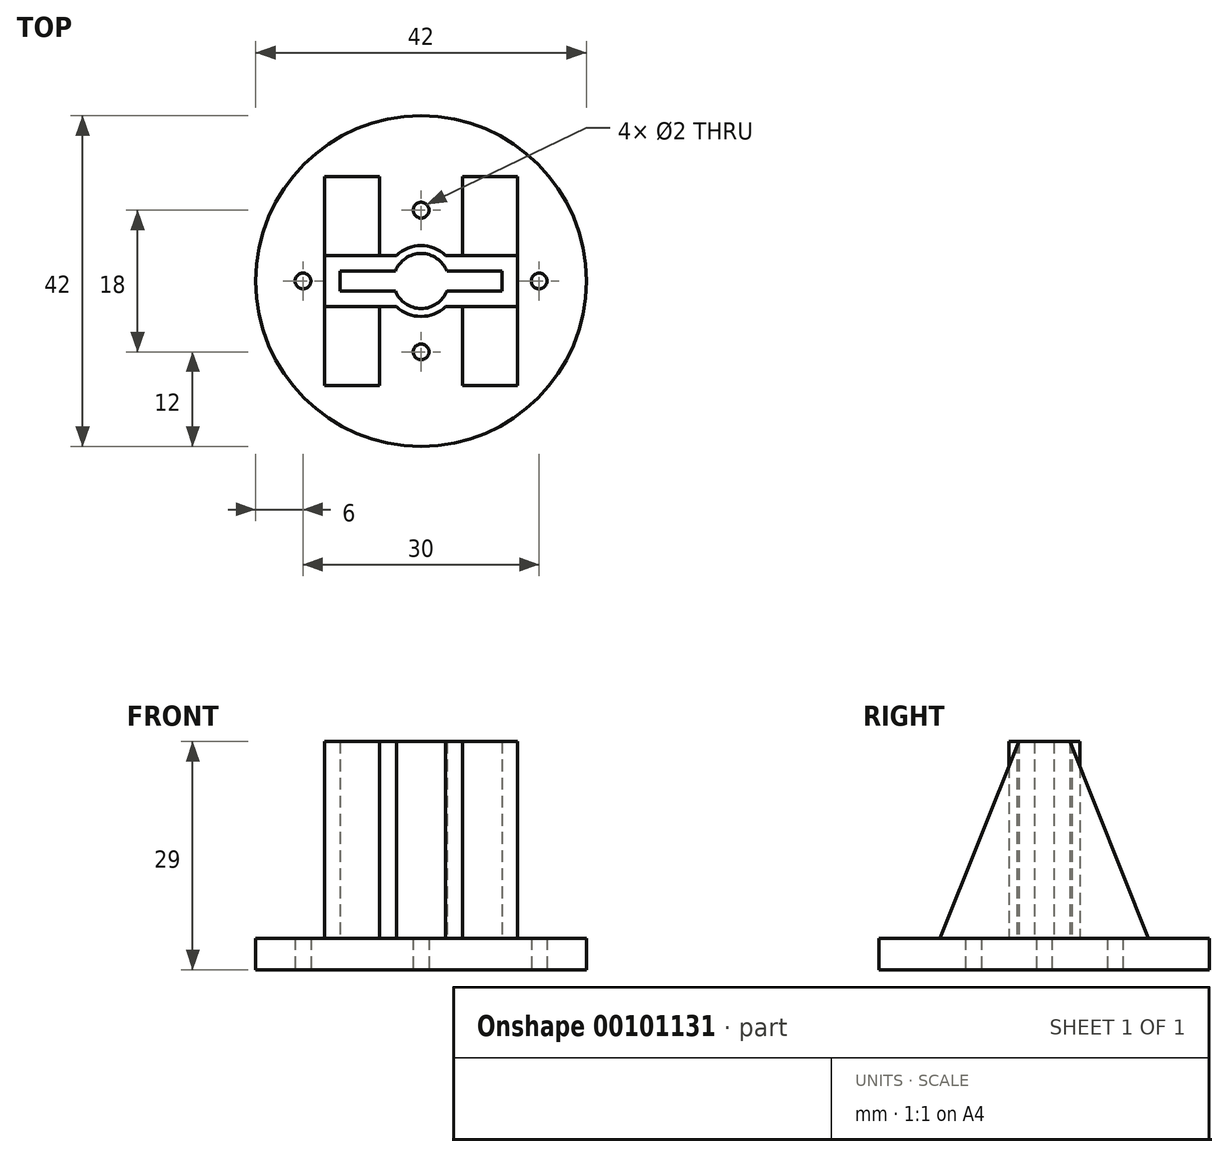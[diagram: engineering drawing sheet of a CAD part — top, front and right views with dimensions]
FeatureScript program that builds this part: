
annotation { "Feature Type Name" : "Feature", "Feature Type Description" : "" }
export const myFeature = defineFeature(function(context is Context, id is Id, definition is map)
    precondition{}
    {
        {
            var Q0;
            Q0=qCreatedBy(makeId("Top.planeOp"),FACE);
            var sketch = newSketch(context, id + "F0", { "sketchPlane" : qUnion([Q0])});
            skPoint(sketch, "E0", {"position": v(0, 9) * mm});
            skPoint(sketch, "E1", {"position": v(-15, 0) * mm});
            skPoint(sketch, "E2", {"position": v(15, 0) * mm});
            skPoint(sketch, "E3", {"position": v(0, -9) * mm});
            skCircle(sketch, "E4", {"center": v(0, 0) * mm, "radius": 21 * mm});
            skSolve(sketch);
        }
        {
            var Q0;
            Q0 = qSketchRegion(id + "F0", true);
            extrude(context, id + "F1", {"entities" : qUnion([Q0]), "depth" : 4 * mm});
        }
        {
            var Q0;
            Q0=sQuery(id+"F0.wireOp",VERTEX,"E1");
            var Q1;
            Q1=sQuery(id+"F0.wireOp",VERTEX,"E3");
            var Q2;
            Q2=sQuery(id+"F0.wireOp",VERTEX,"E0");
            var Q3;
            Q3=sQuery(id+"F0.wireOp",VERTEX,"E2");
            var Q4;
            Q4=makeQuery(id+"F1.opExtrude","SWEPT_BODY",BODY,{"disambiguationData":[OSD([sQuery(id+"F0.wireOp",EDGE,"E4")])]});
            hole(context, id + "F2", {"style" : HoleStyle.SIMPLE, "endStyle" : HoleEndStyle.THROUGH, "oppositeDirection" : true, "holeDiameter" : 2 * mm, "locations" : qUnion([Q0, Q1, Q2, Q3]), "scope" : qUnion([Q4]), "isTappedThrough" : true});
        }
        {
            var Q0;
            Q0=makeQuery(id+"F1.opExtrude","CAP_FACE",FACE,{"disambiguationData":[OSD([sQuery(id+"F0.wireOp",EDGE,"E4")])],"isStart":false});
            var sketch = newSketch(context, id + "F3", { "sketchPlane" : qUnion([Q0])});
            skCircle(sketch, "E5", {"center": v(0, 0) * mm, "radius": 3.5 * mm});
            skLineSegment(sketch, "E6", {"start": v(-3.27, 1.25) * mm, "end": v(-10.27, 1.25) * mm});
            skLineSegment(sketch, "E7", {"start": v(-10.27, 1.25) * mm, "end": v(-10.27, -1.25) * mm});
            skLineSegment(sketch, "E8", {"start": v(-10.27, -1.25) * mm, "end": v(-3.27, -1.25) * mm});
            skLineSegment(sketch, "E9.MirrorCS", {"start": v(3.27, 1.25) * mm, "end": v(10.27, 1.25) * mm});
            skLineSegment(sketch, "E10.MirrorCS", {"start": v(10.27, 1.25) * mm, "end": v(10.27, -1.25) * mm});
            skLineSegment(sketch, "E11.MirrorCS", {"start": v(10.27, -1.25) * mm, "end": v(3.27, -1.25) * mm});
            skCircle(sketch, "E12", {"center": v(0, 0) * mm, "radius": 4.5 * mm});
            skLineSegment(sketch, "E13", {"start": v(-1.3, -3.25) * mm, "end": v(-12.27, -3.25) * mm});
            skLineSegment(sketch, "E14", {"start": v(-12.27, -3.25) * mm, "end": v(-12.27, 3.25) * mm});
            skLineSegment(sketch, "E15", {"start": v(-12.27, 3.25) * mm, "end": v(-1.3, 3.25) * mm});
            skLineSegment(sketch, "E16.MirrorCS", {"start": v(12.27, 3.25) * mm, "end": v(1.3, 3.25) * mm});
            skLineSegment(sketch, "E17.MirrorCS", {"start": v(12.27, -3.25) * mm, "end": v(12.27, 3.25) * mm});
            skLineSegment(sketch, "E18.MirrorCS", {"start": v(1.3, -3.25) * mm, "end": v(12.27, -3.25) * mm});
            skSolve(sketch);
        }
        {
            var Q0;
            {var subQ6=sQuery(id+"F3.wireOp",EDGE,"E7");Q0=makeQuery(id+"F3.imprint","IMPRINT",FACE,{"disambiguationData":[TD([[makeQuery(id+"F3.imprint","IMPRINT",EDGE,{"derivedFrom":subQ6}),-1.0]])]});}
            var Q1;
            {var subQ0=sQuery(id+"F3.wireOp",EDGE,"E15");var subQ1=sQuery(id+"F3.wireOp",EDGE,"E5");var subQ2=makeQuery(id+"F3.imprint","INTERSECT",VERTEX,{"derivedFrom":[subQ1,subQ0]});Q1=makeQuery(id+"F3.imprint","IMPRINT",FACE,{"disambiguationData":[TD([[makeQuery(id+"F3.imprint","IMPRINT",EDGE,{"disambiguationData":[TD([[subQ2,1.0]])],"derivedFrom":subQ1}),-1.0]])]});}
            var Q2;
            {var subQ0=sQuery(id+"F3.wireOp",EDGE,"E6");var subQ1=sQuery(id+"F3.wireOp",EDGE,"E5");var subQ2=makeQuery(id+"F3.imprint","INTERSECT",VERTEX,{"derivedFrom":[subQ1,subQ0]});Q2=makeQuery(id+"F3.imprint","IMPRINT",FACE,{"disambiguationData":[TD([[makeQuery(id+"F3.imprint","IMPRINT",EDGE,{"disambiguationData":[TD([[subQ2,1.0]])],"derivedFrom":subQ1}),-1.0]])]});}
            var Q3;
            {var subQ0=sQuery(id+"F3.wireOp",EDGE,"E8");var subQ1=sQuery(id+"F3.wireOp",EDGE,"E5");var subQ2=makeQuery(id+"F3.imprint","INTERSECT",VERTEX,{"derivedFrom":[subQ1,subQ0]});Q3=makeQuery(id+"F3.imprint","IMPRINT",FACE,{"disambiguationData":[TD([[makeQuery(id+"F3.imprint","IMPRINT",EDGE,{"disambiguationData":[TD([[subQ2,-1.0]])],"derivedFrom":subQ1}),-1.0]])]});}
            var Q4;
            {var subQ0=sQuery(id+"F3.wireOp",EDGE,"E13");var subQ1=sQuery(id+"F3.wireOp",EDGE,"E5");var subQ2=makeQuery(id+"F3.imprint","INTERSECT",VERTEX,{"derivedFrom":[subQ1,subQ0]});Q4=makeQuery(id+"F3.imprint","IMPRINT",FACE,{"disambiguationData":[TD([[makeQuery(id+"F3.imprint","IMPRINT",EDGE,{"disambiguationData":[TD([[subQ2,-1.0]])],"derivedFrom":subQ1}),-1.0]])]});}
            var Q5;
            {var subQ0=sQuery(id+"F3.wireOp",EDGE,"E11.MirrorCS");var subQ1=sQuery(id+"F3.wireOp",EDGE,"E5");var subQ2=makeQuery(id+"F3.imprint","INTERSECT",VERTEX,{"derivedFrom":[subQ1,subQ0]});Q5=makeQuery(id+"F3.imprint","IMPRINT",FACE,{"disambiguationData":[TD([[makeQuery(id+"F3.imprint","IMPRINT",EDGE,{"disambiguationData":[TD([[subQ2,1.0]])],"derivedFrom":subQ1}),-1.0]])]});}
            var Q6;
            {var subQ0=sQuery(id+"F3.wireOp",EDGE,"E9.MirrorCS");var subQ1=sQuery(id+"F3.wireOp",EDGE,"E5");var subQ2=makeQuery(id+"F3.imprint","INTERSECT",VERTEX,{"derivedFrom":[subQ1,subQ0]});Q6=makeQuery(id+"F3.imprint","IMPRINT",FACE,{"disambiguationData":[TD([[makeQuery(id+"F3.imprint","IMPRINT",EDGE,{"disambiguationData":[TD([[subQ2,-1.0]])],"derivedFrom":subQ1}),-1.0]])]});}
            var Q7;
            {var subQ5=sQuery(id+"F3.wireOp",EDGE,"E10.MirrorCS");Q7=makeQuery(id+"F3.imprint","IMPRINT",FACE,{"disambiguationData":[TD([[makeQuery(id+"F3.imprint","IMPRINT",EDGE,{"derivedFrom":subQ5}),1.0]])]});}
            extrude(context, id + "F4", {"entities" : qUnion([Q0, Q1, Q2, Q3, Q4, Q5, Q6, Q7]), "operationType" : NewBodyOperationType.ADD, "depth" : 25 * mm});
        }
        {
            var Q0;
            Q0=makeQuery(id+"F4.opExtrude","SWEPT_FACE",FACE,{"disambiguationData":[OSD([sQuery(id+"F3.wireOp",EDGE,"E17.MirrorCS")])]});
            var sketch = newSketch(context, id + "F5", { "sketchPlane" : qUnion([Q0])});
            skLineSegment(sketch, "E19", {"start": v(-3.25, 29) * mm, "end": v(-13.25, 4) * mm});
            skLineSegment(sketch, "E20", {"start": v(-13.25, 4) * mm, "end": v(-3.25, 4) * mm});
            skLineSegment(sketch, "E21.MirrorCS", {"start": v(3.25, 29) * mm, "end": v(13.25, 4) * mm});
            skLineSegment(sketch, "E22.MirrorCS", {"start": v(13.25, 4) * mm, "end": v(3.25, 4) * mm});
            skSolve(sketch);
        }
        {
            var Q0;
            Q0=makeQuery(id+"F5.imprint","IMPRINT",FACE,{"disambiguationData":[TD([[makeQuery(id+"F5.imprint","IMPRINT",EDGE,{"derivedFrom":sQuery(id+"F5.wireOp",EDGE,"E19")}),1.0]])]});
            var Q1;
            Q1=makeQuery(id+"F5.imprint","IMPRINT",FACE,{"disambiguationData":[TD([[makeQuery(id+"F5.imprint","IMPRINT",EDGE,{"derivedFrom":sQuery(id+"F5.wireOp",EDGE,"E21.MirrorCS")}),-1.0]])]});
            extrude(context, id + "F6", {"entities" : qUnion([Q0, Q1]), "oppositeDirection" : true, "depth" : 7 * mm});
        }
        {
            var Q0;
            Q0=makeQuery(id+"F6.opExtrude","SWEPT_BODY",BODY,{"disambiguationData":[OSD([sQuery(id+"F3.wireOp",EDGE,"E17.MirrorCS"),sQuery(id+"F3.wireOp",EDGE,"E18.MirrorCS"),sQuery(id+"F5.wireOp",EDGE,"E19"),sQuery(id+"F5.wireOp",EDGE,"E20")])]});
            var Q1;
            Q1=makeQuery(id+"F6.opExtrude","SWEPT_BODY",BODY,{"disambiguationData":[OSD([sQuery(id+"F3.wireOp",EDGE,"E16.MirrorCS"),sQuery(id+"F3.wireOp",EDGE,"E17.MirrorCS"),sQuery(id+"F5.wireOp",EDGE,"E21.MirrorCS"),sQuery(id+"F5.wireOp",EDGE,"E22.MirrorCS")])]});
            var Q2;
            Q2=qCreatedBy(makeId("Right.planeOp"),FACE);
            mirror(context, id + "F7", {"operationType" : NewBodyOperationType.ADD, "entities" : qUnion([Q0, Q1]), "mirrorPlane" : qUnion([Q2])});
        }
    });
